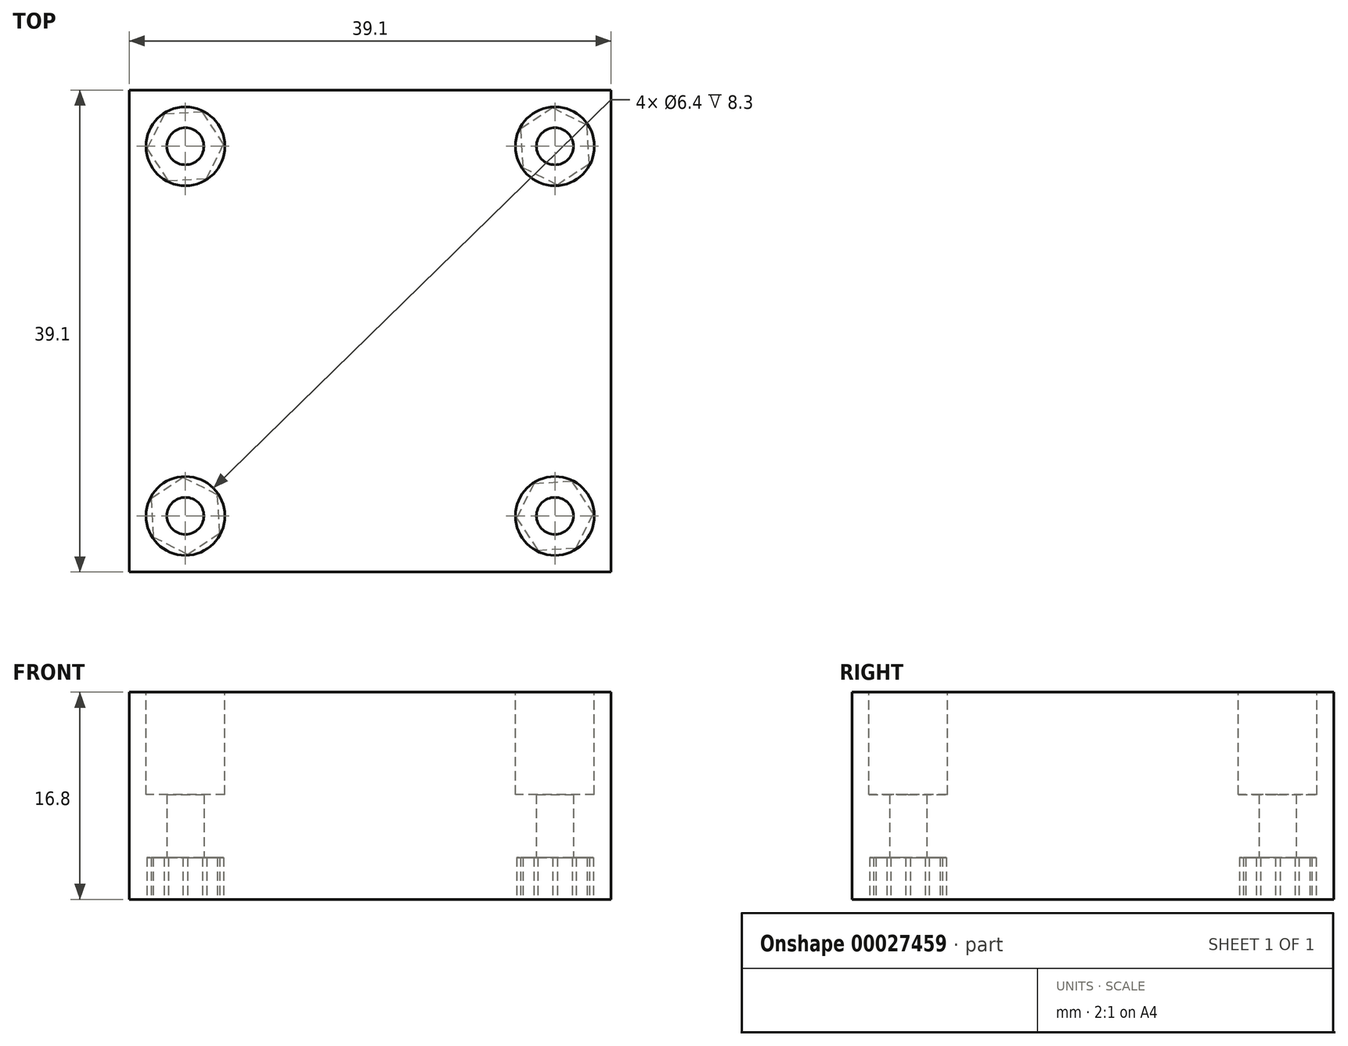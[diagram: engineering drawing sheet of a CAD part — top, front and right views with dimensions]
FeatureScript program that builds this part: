
annotation { "Feature Type Name" : "Feature", "Feature Type Description" : "" }
export const myFeature = defineFeature(function(context is Context, id is Id, definition is map)
    precondition{}
    {
        {
            var Q0;
            Q0=qCreatedBy(makeId("Top.planeOp"),FACE);
            var sketch = newSketch(context, id + "F0", { "sketchPlane" : qUnion([Q0])});
            skLineSegment(sketch, "E0.rect.bottom", {"start": v(-19.55, 19.55) * mm, "end": v(19.55, 19.55) * mm});
            skLineSegment(sketch, "E0.rect.top", {"start": v(-19.55, -19.55) * mm, "end": v(19.55, -19.55) * mm});
            skLineSegment(sketch, "E0.rect.left", {"start": v(-19.55, 19.55) * mm, "end": v(-19.55, -19.55) * mm});
            skLineSegment(sketch, "E0.rect.right", {"start": v(19.55, 19.55) * mm, "end": v(19.55, -19.55) * mm});
            skPoint(sketch, "E0.rect.middle", {"position": v(0, 0) * mm});
            skCircle(sketch, "E1", {"center": v(0, 0) * mm, "radius": 21.2 * mm, "construction": true});
            skLineSegment(sketch, "E2", {"start": v(19.55, 19.55) * mm, "end": v(-19.55, -19.55) * mm, "construction": true});
            skLineSegment(sketch, "E3", {"start": v(19.55, -19.55) * mm, "end": v(-19.55, 19.55) * mm, "construction": true});
            skCircle(sketch, "E4", {"center": v(-15, 15) * mm, "radius": 1.5 * mm});
            skLineSegment(sketch, "E5", {"start": v(0, 19.55) * mm, "end": v(0, -19.55) * mm, "construction": true});
            skLineSegment(sketch, "E6", {"start": v(-19.55, 0) * mm, "end": v(19.55, 0) * mm, "construction": true});
            skCircle(sketch, "E7.1.0", {"center": v(-15, -15) * mm, "radius": 1.5 * mm});
            skCircle(sketch, "E7.2.0", {"center": v(15, -15) * mm, "radius": 1.5 * mm});
            skCircle(sketch, "E7.3.0", {"center": v(15, 15) * mm, "radius": 1.5 * mm});
            skSolve(sketch);
        }
        {
            var Q0;
            Q0=makeQuery(id+"F0.imprint","IMPRINT",FACE,{"disambiguationData":[TD([[makeQuery(id+"F0.imprint","IMPRINT",EDGE,{"derivedFrom":sQuery(id+"F0.wireOp",EDGE,"E0.rect.bottom")}),-1.0]])]});
            extrude(context, id + "F1", {"entities" : qUnion([Q0]), "depth" : 16.8 * mm});
        }
        {
            var Q0;
            Q0=makeQuery(id+"F1.opExtrude","CAP_FACE",FACE,{"disambiguationData":[OSD([sQuery(id+"F0.wireOp",EDGE,"E0.rect.bottom"),sQuery(id+"F0.wireOp",EDGE,"E0.rect.top"),sQuery(id+"F0.wireOp",EDGE,"E0.rect.left"),sQuery(id+"F0.wireOp",EDGE,"E0.rect.right"),sQuery(id+"F0.wireOp",EDGE,"E4"),sQuery(id+"F0.wireOp",EDGE,"E7.1.0"),sQuery(id+"F0.wireOp",EDGE,"E7.2.0"),sQuery(id+"F0.wireOp",EDGE,"E7.3.0")])],"isStart":false});
            var sketch = newSketch(context, id + "F2", { "sketchPlane" : qUnion([Q0])});
            skCircle(sketch, "E8", {"center": v(-15, 15) * mm, "radius": 3.2 * mm});
            skCircle(sketch, "E9.1.0", {"center": v(-15, -15) * mm, "radius": 3.2 * mm});
            skCircle(sketch, "E9.2.0", {"center": v(15, -15) * mm, "radius": 3.2 * mm});
            skCircle(sketch, "E9.3.0", {"center": v(15, 15) * mm, "radius": 3.2 * mm});
            skPoint(sketch, "E9.center", {"position": v(0, 0) * mm});
            skSolve(sketch);
        }
        {
            var Q0;
            Q0=qSketchRegion(id+"F2",true);
            extrude(context, id + "F3", {"entities" : qUnion([Q0]), "operationType" : NewBodyOperationType.REMOVE, "oppositeDirection" : true, "depth" : 8.3 * mm});
        }
        {
            var Q0;
            Q0=makeQuery(id+"F1.opExtrude","CAP_FACE",FACE,{"disambiguationData":[OSD([sQuery(id+"F0.wireOp",EDGE,"E0.rect.bottom"),sQuery(id+"F0.wireOp",EDGE,"E0.rect.top"),sQuery(id+"F0.wireOp",EDGE,"E0.rect.left"),sQuery(id+"F0.wireOp",EDGE,"E0.rect.right"),sQuery(id+"F0.wireOp",EDGE,"E4"),sQuery(id+"F0.wireOp",EDGE,"E7.1.0"),sQuery(id+"F0.wireOp",EDGE,"E7.2.0"),sQuery(id+"F0.wireOp",EDGE,"E7.3.0")])],"isStart":true});
            var sketch = newSketch(context, id + "F4", { "sketchPlane" : qUnion([Q0])});
            skCircle(sketch, "E10.cCircle", {"center": v(-15, -15) * mm, "radius": 2.7 * mm, "construction": true});
            skLineSegment(sketch, "E10.0", {"start": v(-13.27, -12.39) * mm, "end": v(-11.88, -15.18) * mm});
            skLineSegment(sketch, "E10.1", {"start": v(-11.88, -15.18) * mm, "end": v(-13.6, -17.78) * mm});
            skLineSegment(sketch, "E10.2", {"start": v(-13.6, -17.78) * mm, "end": v(-16.7, -17.6) * mm});
            skLineSegment(sketch, "E10.3", {"start": v(-16.7, -17.6) * mm, "end": v(-18.1, -14.8) * mm});
            skLineSegment(sketch, "E10.4", {"start": v(-18.1, -14.8) * mm, "end": v(-16.38, -12.2) * mm});
            skLineSegment(sketch, "E10.5", {"start": v(-16.38, -12.2) * mm, "end": v(-13.27, -12.39) * mm});
            skPoint(sketch, "E10.0.midPoint", {"position": v(-12.58, -13.78) * mm});
            skPoint(sketch, "E11.1.6", {"position": v(13.78, -12.58) * mm});
            skCircle(sketch, "E11.1.7", {"center": v(15, -15) * mm, "radius": 2.7 * mm, "construction": true});
            skLineSegment(sketch, "E11.1.8", {"start": v(12.39, -13.27) * mm, "end": v(15.18, -11.88) * mm});
            skLineSegment(sketch, "E11.1.10", {"start": v(15.18, -11.88) * mm, "end": v(17.78, -13.6) * mm});
            skLineSegment(sketch, "E11.1.12", {"start": v(17.78, -13.6) * mm, "end": v(17.6, -16.7) * mm});
            skLineSegment(sketch, "E11.1.14", {"start": v(17.6, -16.7) * mm, "end": v(14.8, -18.1) * mm});
            skLineSegment(sketch, "E11.1.16", {"start": v(14.8, -18.1) * mm, "end": v(12.2, -16.38) * mm});
            skLineSegment(sketch, "E11.1.18", {"start": v(12.2, -16.38) * mm, "end": v(12.39, -13.27) * mm});
            skPoint(sketch, "E11.2.6", {"position": v(12.58, 13.78) * mm});
            skCircle(sketch, "E11.2.7", {"center": v(15, 15) * mm, "radius": 2.7 * mm, "construction": true});
            skLineSegment(sketch, "E11.2.8", {"start": v(13.27, 12.39) * mm, "end": v(11.88, 15.18) * mm});
            skLineSegment(sketch, "E11.2.10", {"start": v(11.88, 15.18) * mm, "end": v(13.6, 17.78) * mm});
            skLineSegment(sketch, "E11.2.12", {"start": v(13.6, 17.78) * mm, "end": v(16.7, 17.6) * mm});
            skLineSegment(sketch, "E11.2.14", {"start": v(16.7, 17.6) * mm, "end": v(18.1, 14.8) * mm});
            skLineSegment(sketch, "E11.2.16", {"start": v(18.1, 14.8) * mm, "end": v(16.38, 12.2) * mm});
            skLineSegment(sketch, "E11.2.18", {"start": v(16.38, 12.2) * mm, "end": v(13.27, 12.39) * mm});
            skPoint(sketch, "E11.3.6", {"position": v(-13.78, 12.58) * mm});
            skCircle(sketch, "E11.3.7", {"center": v(-15, 15) * mm, "radius": 2.7 * mm, "construction": true});
            skLineSegment(sketch, "E11.3.8", {"start": v(-12.39, 13.27) * mm, "end": v(-15.18, 11.88) * mm});
            skLineSegment(sketch, "E11.3.10", {"start": v(-15.18, 11.88) * mm, "end": v(-17.78, 13.6) * mm});
            skLineSegment(sketch, "E11.3.12", {"start": v(-17.78, 13.6) * mm, "end": v(-17.6, 16.7) * mm});
            skLineSegment(sketch, "E11.3.14", {"start": v(-17.6, 16.7) * mm, "end": v(-14.8, 18.1) * mm});
            skLineSegment(sketch, "E11.3.16", {"start": v(-14.8, 18.1) * mm, "end": v(-12.2, 16.38) * mm});
            skLineSegment(sketch, "E11.3.18", {"start": v(-12.2, 16.38) * mm, "end": v(-12.39, 13.27) * mm});
            skPoint(sketch, "E11.center", {"position": v(0, 0) * mm});
            skSolve(sketch);
        }
        {
            var Q0;
            Q0=qSketchRegion(id+"F4",true);
            extrude(context, id + "F5", {"entities" : qUnion([Q0]), "operationType" : NewBodyOperationType.REMOVE, "oppositeDirection" : true, "depth" : 3.4 * mm});
        }
    });
